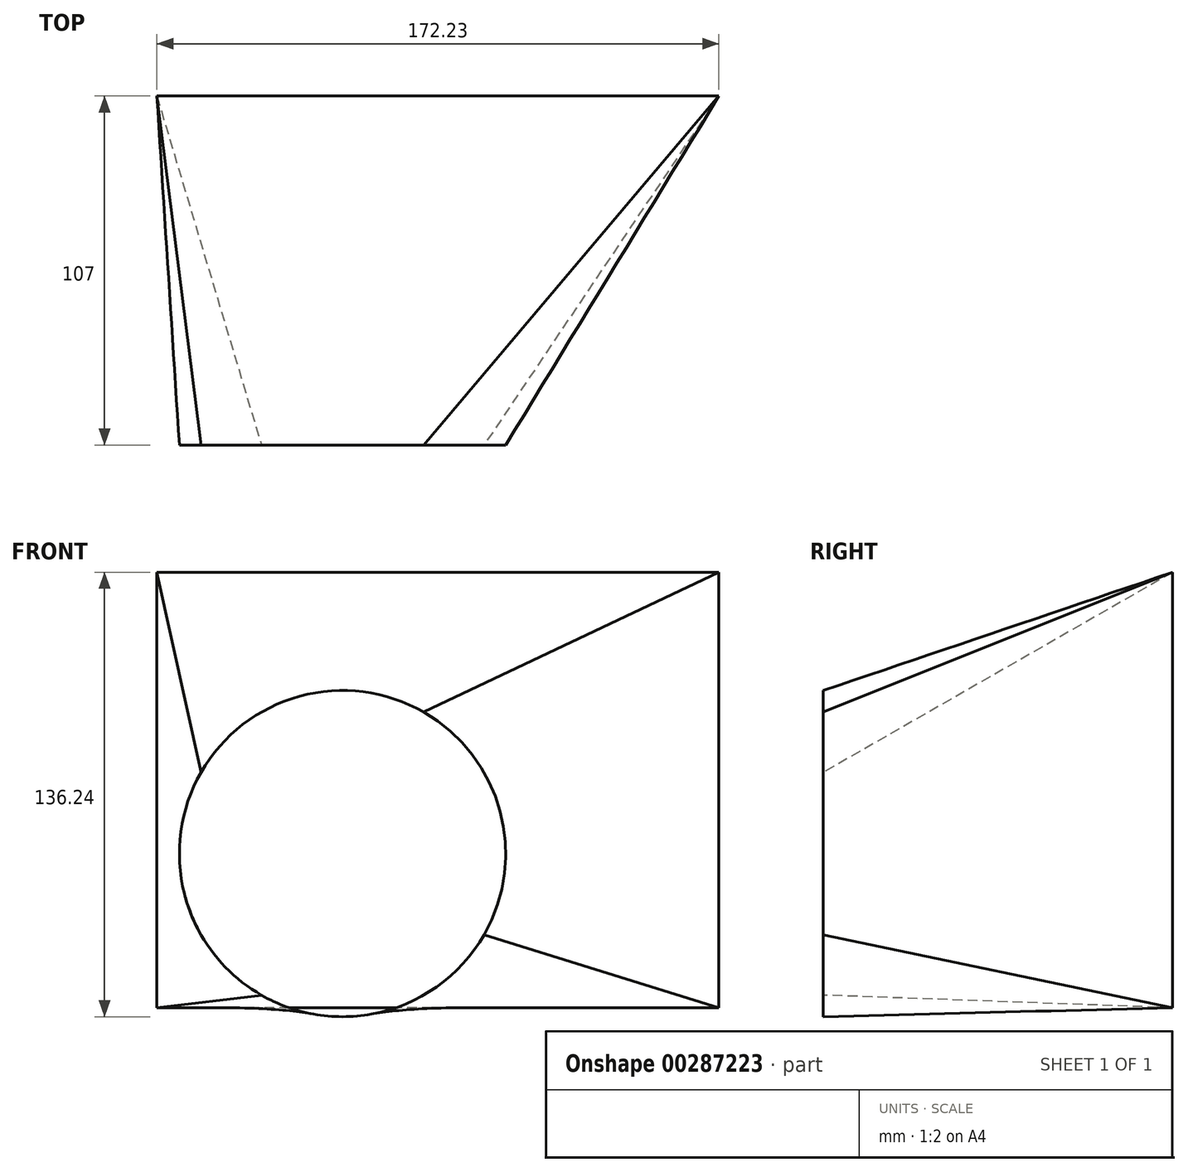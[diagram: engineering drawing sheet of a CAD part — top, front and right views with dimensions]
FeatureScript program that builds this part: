
annotation { "Feature Type Name" : "Feature", "Feature Type Description" : "" }
export const myFeature = defineFeature(function(context is Context, id is Id, definition is map)
    precondition{}
    {
        {
            var Q0;
            Q0=qCreatedBy(makeId("Front.planeOp"),FACE);
            var sketch = newSketch(context, id + "F0", { "sketchPlane" : qUnion([Q0])});
            skLineSegment(sketch, "E0", {"start": v(0, 0) * mm, "end": v(0, 89.51) * mm});
            skLineSegment(sketch, "E1.bottom", {"start": v(-169.78, 0) * mm, "end": v(-342, 0) * mm});
            skLineSegment(sketch, "E1.top", {"start": v(-169.78, 133.5) * mm, "end": v(-342, 133.5) * mm});
            skLineSegment(sketch, "E1.left", {"start": v(-169.78, 0) * mm, "end": v(-169.78, 133.5) * mm});
            skLineSegment(sketch, "E1.right", {"start": v(-342, 0) * mm, "end": v(-342, 133.5) * mm});
            skCircle(sketch, "E2", {"center": v(-81.3, 43.56) * mm, "radius": 43.56 * mm});
            skPoint(sketch, "E2.first.point", {"position": v(-81.3, 0) * mm});
            skPoint(sketch, "E2.second.point", {"position": v(-114.42, 71.84) * mm});
            skPoint(sketch, "E2.third.point", {"position": v(-64.7, 83.83) * mm});
            skLineSegment(sketch, "E3", {"start": v(-403.13, 314.58) * mm, "end": v(181.28, 314.58) * mm, "construction": true});
            skSolve(sketch);
        }
        {
            var Q0;
            Q0=qCreatedBy(makeId("Top.planeOp"),FACE);
            var sketch = newSketch(context, id + "F1", { "sketchPlane" : qUnion([Q0])});
            skLineSegment(sketch, "E4", {"start": v(0, 0) * mm, "end": v(0, -117.21) * mm});
            skLineSegment(sketch, "E5", {"start": v(6.16, -131.65) * mm, "end": v(59.57, -182.85) * mm});
            skLineSegment(sketch, "E6", {"start": v(71.89, -211.73) * mm, "end": v(71.89, -336.48) * mm});
            skPoint(sketch, "E7.visualSharp", {"position": v(0, -125.75) * mm});
            skArc(sketch, "E7.filletArc", {"start": v(0, -117.21) * mm, "mid": v(1.6, -125.06) * mm, "end": v(6.16, -131.65) * mm});
            skPoint(sketch, "E8.visualSharp", {"position": v(71.89, -194.66) * mm});
            skArc(sketch, "E8.filletArc", {"start": v(71.89, -211.73) * mm, "mid": v(68.68, -196.03) * mm, "end": v(59.57, -182.85) * mm});
            skArc(sketch, "E9", {"start": v(71.89, -336.48) * mm, "mid": v(106.24, -453.85) * mm, "end": v(198.47, -534.17) * mm});
            skLineSegment(sketch, "E10", {"start": v(198.47, -534.17) * mm, "end": v(309.15, -585.16) * mm});
            skSolve(sketch);
        }
        {
            var Q0;
            Q0=qCreatedBy(makeId("Front.planeOp"),FACE);
            cPlane(context, id + "F2", {"entities" : qUnion([Q0]), "cplaneType" : CPlaneType.OFFSET, "offset" : 107 * mm, "width" : 150 * mm, "height" : 150 * mm});
        }
        {
            var Q0;
            Q0=qCreatedBy(id+"F2.planeOp",FACE);
            var sketch = newSketch(context, id + "F3", { "sketchPlane" : qUnion([Q0])});
            skLineSegment(sketch, "E11", {"start": v(-328.49, 72.11) * mm, "end": v(-241.72, 22.4) * mm, "construction": true});
            skLineSegment(sketch, "E12", {"start": v(-260.25, 90.65) * mm, "end": v(-309.96, 3.88) * mm, "construction": true});
            skArc(sketch, "E13", {"start": v(-241.72, 22.4) * mm, "mid": v(-236.85, 60.36) * mm, "end": v(-260.25, 90.65) * mm});
            skArc(sketch, "E14", {"start": v(-309.96, 3.88) * mm, "mid": v(-272, -1) * mm, "end": v(-241.72, 22.4) * mm});
            skArc(sketch, "E15", {"start": v(-260.25, 90.65) * mm, "mid": v(-298.2, 95.51) * mm, "end": v(-328.49, 72.11) * mm});
            skArc(sketch, "E16", {"start": v(-328.49, 72.11) * mm, "mid": v(-333.36, 34.16) * mm, "end": v(-309.96, 3.88) * mm});
            skSolve(sketch);
        }
        {
            var Q0;
            Q0=sQuery(id+"F0.wireOp",EDGE,"E1.top");
            var Q1;
            Q1=sQuery(id+"F3.wireOp",EDGE,"E15");
            loft(context, id + "F4", {"bodyType" : ToolBodyType.SURFACE, "wireProfilesArray" : [{ "wireProfileEntities" : qUnion([Q0]) }, { "wireProfileEntities" : qUnion([Q1]) }]});
        }
        {
            var Q0;
            Q0=sQuery(id+"F0.wireOp",EDGE,"E1.left");
            var Q1;
            Q1=sQuery(id+"F3.wireOp",EDGE,"E13");
            loft(context, id + "F5", {"bodyType" : ToolBodyType.SURFACE, "wireProfilesArray" : [{ "wireProfileEntities" : qUnion([Q0]) }, { "wireProfileEntities" : qUnion([Q1]) }]});
        }
        {
            var Q0;
            Q0=sQuery(id+"F0.wireOp",EDGE,"E1.bottom");
            var Q1;
            Q1=sQuery(id+"F3.wireOp",EDGE,"E14");
            loft(context, id + "F6", {"bodyType" : ToolBodyType.SURFACE, "wireProfilesArray" : [{ "wireProfileEntities" : qUnion([Q0]) }, { "wireProfileEntities" : qUnion([Q1]) }]});
        }
        {
            var Q0;
            Q0=sQuery(id+"F0.wireOp",EDGE,"E1.right");
            var Q1;
            Q1=sQuery(id+"F3.wireOp",EDGE,"E16");
            loft(context, id + "F7", {"bodyType" : ToolBodyType.SURFACE, "wireProfilesArray" : [{ "wireProfileEntities" : qUnion([Q0]) }, { "wireProfileEntities" : qUnion([Q1]) }]});
        }
    });
